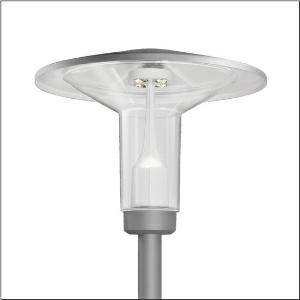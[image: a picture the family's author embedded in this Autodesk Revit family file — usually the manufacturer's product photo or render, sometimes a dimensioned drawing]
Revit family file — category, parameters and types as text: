
# Revit family: laterne_iq___st1_2a_5xa5255ef14h_6af0
name_source: partatom
category: Lighting Fixtures
units: mm (PartAtom-declared; Revit-internal decimal feet)

## family parameters
Cut with Voids When Loaded = No
Host = Face
Light Source = No
Part Type = Normal
Room Calculation Point = No
Round Connector Dimension = Use Diameter
Shared = No

## types (1)
- --- (1 x LED, 1540 lm, 10.5 W, 3000K)
    Apparent Load = 11 VA
    CIE Flux Codes = 25 63 94 98 100
    Color Rendering = 70
    Color Temperature = 3000K
    Default Elevation = 1800 mm
    Description = Lantern iQ, mast luminaire, Module 540 iQ-SR, primary light control with 3 zone facetted reflector, of plastic, silver coated, highly specular, structured, primary optical cover: cover, of PMMA, transparent, light distribution: ST1.2a, light emission: direct distribution, primary light characteristic: asymmetric, installation type: post-top, LED, High Power LED, rated luminous flux: 1.540lm, luminous efficacy: 147lm/W, light colour: 730, colour temperature: 3000K, control gear: ECG iQ, control: Auto-Match, Temp-Guard, Lumen-Switch, Night-Set, Smart-Wire, Light-Fading, Desk-Remote (wireless, voltage-free reading and setting of iQ features in the workshop via application-optimized NFC function/RFID function), optimised constant luminous flux control (CLO 2.0), Street-Remote, presetting dimming logarithmic, with terminal, 6-pole, max. 2.5mm², mains connection: 230..240V, AC, 50/60Hz, start of lifetime: 11W, end of service life: 11W, reduction: 5W, luminaire housing, upper part, of glass-fibre reinforced polyester, coated, Siteco® metallic grey (DB 702S), diameter: 750mm, height: 583mm, spigot size: d x l = 76 x 70mm (post-top) | with reducer (optional accessory) 60 x 70mm, post-top mast mounting element, of diecast aluminium, coated, Siteco® metallic grey (DB 702S), Module 540 iQ-SR, traffic white (RAL 9016), equipment: standard, protection rating (complete): IP65, insulation class (complete): insulation class II (safety insulation), certification: CE, ENEC, VDE, packaging unit: 1 piece

Light Distribution: ST1.2a
    Height = 583 mm
    Lamp = 1 x LED
    Lamp Light Flux = 1540 lm
    Lamp Power = 10.5 W
    Lamp count = 1
    Length = 750 mm
    Luminous efficacy = 147 lm/W
    Manufacturer = Siteco
    ModVariant = No
    Model = 5XA5255EF14H
    Number of Poles = 1
    OnlyDefault = Yes
    Power Factor = 1
    Product Name = Laterne iQ | ST1.2a
    Product group = mast luminaire | pylon top
    ProductGroupID = 6100
    Protection Class = Protection class II
    Protection Degree = IP 65
    RLX_Detail_Level = 1
    RLX_Emergency_Light_Flux = 0 lm
    RLX_Emergency_Type = 0
    RLX_Emergency_Type_DB = No
    RlxData = <blob elided: 103185 chars, md5=73ac647d>
    Socket = socket
    Standby Power = 0 W
    System Light Flux = 1540 lm
    System Power = 11 W
    Type Comments = factory setting: luminous flux: 100 % | dim-lin: 254 | 419 mA
    Type Image = l_1006050.jpg
    URL = http://relux.com
    VarID = @adj_110811
    Voltage = 0 V
    Weight = 0.00 kg
    Width = 0 mm  [stored 0 ft]

note: [stored X ft] marks values corroborated as IEEE doubles in the binary element streams (Revit-internal decimal feet)

## geometry (parser evidence)
native form markers: Blend x4, Sweep x12
no freeform markers — native parametric forms only
